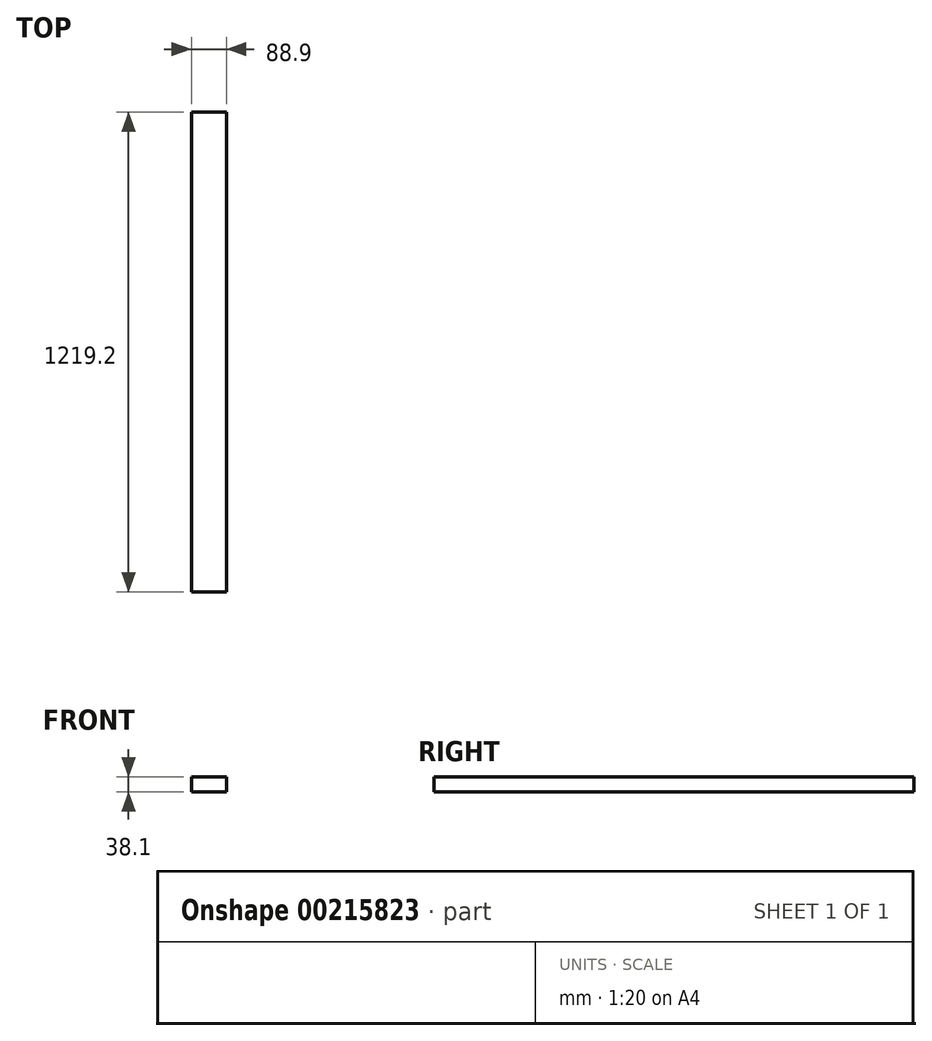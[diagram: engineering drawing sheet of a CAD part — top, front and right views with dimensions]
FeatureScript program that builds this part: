
annotation { "Feature Type Name" : "Feature", "Feature Type Description" : "" }
export const myFeature = defineFeature(function(context is Context, id is Id, definition is map)
    precondition{}
    {
        {
            var Q0;
            Q0=qCreatedBy(makeId("Front.planeOp"),FACE);
            var sketch = newSketch(context, id + "F0", { "sketchPlane" : qUnion([Q0])});
            skLineSegment(sketch, "E0.bottom", {"start": v(44.45, 19.05) * mm, "end": v(-44.45, 19.05) * mm});
            skLineSegment(sketch, "E0.top", {"start": v(44.45, -19.05) * mm, "end": v(-44.45, -19.05) * mm});
            skLineSegment(sketch, "E0.left", {"start": v(44.45, 19.05) * mm, "end": v(44.45, -19.05) * mm});
            skLineSegment(sketch, "E0.right", {"start": v(-44.45, 19.05) * mm, "end": v(-44.45, -19.05) * mm});
            skPoint(sketch, "E0.middle", {"position": v(0, 0) * mm});
            skSolve(sketch);
        }
        {
            var Q0;
            Q0=makeQuery(id+"F0.imprint","IMPRINT",FACE,{"disambiguationData":[TD([[makeQuery(id+"F0.imprint","IMPRINT",EDGE,{"derivedFrom":sQuery(id+"F0.wireOp",EDGE,"E0.bottom")}),1.0]])]});
            extrude(context, id + "F1", {"entities" : qUnion([Q0]), "depth" : 609.6 * mm, "hasSecondDirection" : true, "secondDirectionOppositeDirection" : true, "secondDirectionDepth" : 609.6 * mm});
        }
    });
